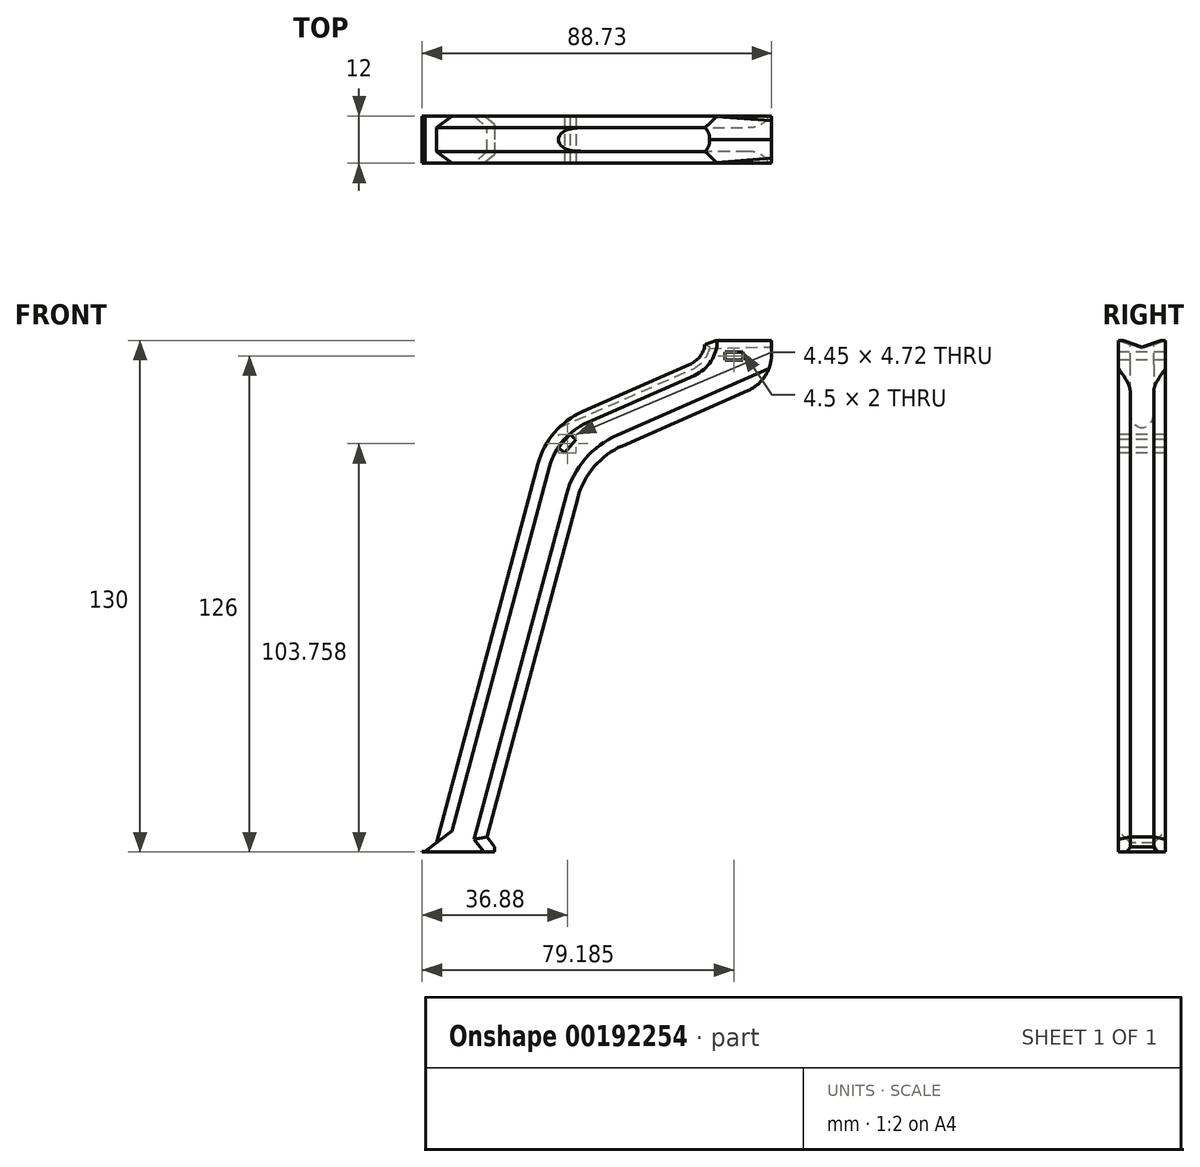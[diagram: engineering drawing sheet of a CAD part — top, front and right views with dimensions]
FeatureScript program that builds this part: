
annotation { "Feature Type Name" : "Feature", "Feature Type Description" : "" }
export const myFeature = defineFeature(function(context is Context, id is Id, definition is map)
    precondition{}
    {
        {
            var Q0;
            Q0=qCreatedBy(makeId("Front.planeOp"),FACE);
            var sketch = newSketch(context, id + "F0", { "sketchPlane" : qUnion([Q0])});
            skLineSegment(sketch, "E0", {"start": v(0, 0) * mm, "end": v(-12.42, 0) * mm});
            skLineSegment(sketch, "E1", {"start": v(-12.42, 0) * mm, "end": v(16.52, 108) * mm});
            skLineSegment(sketch, "E2", {"start": v(16.52, 108) * mm, "end": v(52.49, 123.83) * mm});
            skLineSegment(sketch, "E3", {"start": v(66.52, 130) * mm, "end": v(96.31, 130) * mm});
            skLineSegment(sketch, "E4", {"start": v(96.31, 130) * mm, "end": v(26.62, 99.33) * mm});
            skLineSegment(sketch, "E5", {"start": v(26.62, 99.33) * mm, "end": v(0, 0) * mm});
            skLineSegment(sketch, "E6", {"start": v(66.52, 130) * mm, "end": v(-16.13, 130) * mm, "construction": true});
            skCircle(sketch, "E7", {"center": v(49.77, 130) * mm, "radius": 6.74 * mm});
            skLineSegment(sketch, "E8", {"start": v(66.52, 130) * mm, "end": v(56.52, 130) * mm});
            skSolve(sketch);
        }
        {
            var Q0;
            Q0=makeQuery(id+"F0.imprint","IMPRINT",FACE,{"disambiguationData":[TD([[makeQuery(id+"F0.imprint","IMPRINT",EDGE,{"derivedFrom":sQuery(id+"F0.wireOp",EDGE,"E0")}),-1.0]])]});
            extrude(context, id + "F1", {"entities" : qUnion([Q0]), "depth" : 12 * mm});
        }
        {
            var Q0;
            Q0=makeQuery(id+"F1.opExtrude","CAP_FACE",FACE,{"disambiguationData":[OSD([sQuery(id+"F0.wireOp",EDGE,"E0"),sQuery(id+"F0.wireOp",EDGE,"E1"),sQuery(id+"F0.wireOp",EDGE,"E2"),sQuery(id+"F0.wireOp",EDGE,"E3"),sQuery(id+"F0.wireOp",EDGE,"E4"),sQuery(id+"F0.wireOp",EDGE,"E5")])],"isStart":false});
            var sketch = newSketch(context, id + "F2", { "sketchPlane" : qUnion([Q0])});
            skLineSegment(sketch, "E9.0.0", {"start": v(-12.42, 0) * mm, "end": v(0, 0) * mm});
            skLineSegment(sketch, "E9.0.1", {"start": v(0, 0) * mm, "end": v(26.62, 99.33) * mm});
            skLineSegment(sketch, "E9.0.2", {"start": v(26.62, 99.33) * mm, "end": v(96.31, 130) * mm});
            skLineSegment(sketch, "E9.0.3", {"start": v(96.31, 130) * mm, "end": v(56.52, 130) * mm});
            skLineSegment(sketch, "E9.0.4", {"start": v(66.52, 130) * mm, "end": v(16.52, 108) * mm});
            skLineSegment(sketch, "E9.0.5", {"start": v(16.52, 108) * mm, "end": v(-12.42, 0) * mm});
            skLineSegment(sketch, "E10", {"start": v(84.27, 124.7) * mm, "end": v(54.47, 124.7) * mm});
            skSolve(sketch);
        }
        {
            var Q0;
            Q0=makeQuery(id+"F1.opExtrude","CAP_FACE",FACE,{"disambiguationData":[OSD([sQuery(id+"F0.wireOp",EDGE,"E0"),sQuery(id+"F0.wireOp",EDGE,"E1"),sQuery(id+"F0.wireOp",EDGE,"E2"),sQuery(id+"F0.wireOp",EDGE,"E3"),sQuery(id+"F0.wireOp",EDGE,"E4"),sQuery(id+"F0.wireOp",EDGE,"E5")])],"isStart":false});
            var sketch = newSketch(context, id + "F3", { "sketchPlane" : qUnion([Q0])});
            skPoint(sketch, "E11.endSnap0", {"position": v(34.5, 115.91) * mm});
            skLineSegment(sketch, "E12", {"start": v(22.17, 106.12) * mm, "end": v(23.68, 104.81) * mm});
            skLineSegment(sketch, "E13", {"start": v(23.68, 104.81) * mm, "end": v(20.75, 101.4) * mm});
            skLineSegment(sketch, "E14", {"start": v(20.75, 101.4) * mm, "end": v(19.24, 102.7) * mm});
            skLineSegment(sketch, "E15", {"start": v(19.24, 102.7) * mm, "end": v(22.17, 106.12) * mm});
            skPoint(sketch, "E16", {"position": v(22.17, 106.12) * mm});
            skPoint(sketch, "E17.orphan", {"position": v(18.8, 109) * mm});
            skLineSegment(sketch, "E18", {"start": v(16.52, 108) * mm, "end": v(33.3, 93.6) * mm, "construction": true});
            skSolve(sketch);
        }
        {
            var Q0;
            Q0=makeQuery(id+"F3.imprint","IMPRINT",FACE,{"disambiguationData":[TD([[makeQuery(id+"F3.imprint","IMPRINT",EDGE,{"derivedFrom":sQuery(id+"F3.wireOp",EDGE,"E12")}),-1.0]])]});
            extrude(context, id + "F4", {"entities" : qUnion([Q0]), "operationType" : NewBodyOperationType.REMOVE, "oppositeDirection" : true, "depth" : 25 * mm});
        }
        {
            var Q0;
            Q0=makeQuery(id+"F1.opExtrude","CAP_FACE",FACE,{"disambiguationData":[OSD([sQuery(id+"F0.wireOp",EDGE,"E0"),sQuery(id+"F0.wireOp",EDGE,"E1"),sQuery(id+"F0.wireOp",EDGE,"E2"),sQuery(id+"F0.wireOp",EDGE,"E3"),sQuery(id+"F0.wireOp",EDGE,"E4"),sQuery(id+"F0.wireOp",EDGE,"E5")])],"isStart":false});
            var sketch = newSketch(context, id + "F5", { "sketchPlane" : qUnion([Q0])});
            skLineSegment(sketch, "E19.0", {"start": v(61.52, 130) * mm, "end": v(73.52, 130) * mm});
            skLineSegment(sketch, "E20.0", {"start": v(81.02, 130) * mm, "end": v(85.52, 130) * mm});
            skLineSegment(sketch, "E21.bottom", {"start": v(61.52, 127) * mm, "end": v(66.02, 127) * mm});
            skLineSegment(sketch, "E21.top", {"start": v(61.52, 125) * mm, "end": v(66.02, 125) * mm});
            skLineSegment(sketch, "E21.left", {"start": v(61.52, 127) * mm, "end": v(61.52, 125) * mm});
            skLineSegment(sketch, "E21.right", {"start": v(66.02, 127) * mm, "end": v(66.02, 125) * mm});
            skSolve(sketch);
        }
        {
            var Q0;
            Q0=makeQuery(id+"F5.imprint","IMPRINT",FACE,{"disambiguationData":[TD([[makeQuery(id+"F5.imprint","IMPRINT",EDGE,{"derivedFrom":sQuery(id+"F5.wireOp",EDGE,"E21.bottom")}),-1.0]])]});
            extrude(context, id + "F6", {"entities" : qUnion([Q0]), "operationType" : NewBodyOperationType.REMOVE, "oppositeDirection" : true, "depth" : 25 * mm});
        }
        {
            var Q0;
            Q0=makeQuery(id+"F1.opExtrude","SWEPT_FACE",FACE,{"disambiguationData":[OSD([sQuery(id+"F0.wireOp",EDGE,"E0")])]});
            var sketch = newSketch(context, id + "F7", { "sketchPlane" : qUnion([Q0])});
            skLineSegment(sketch, "E22.bottom", {"start": v(3, 0) * mm, "end": v(-15.42, 0) * mm});
            skLineSegment(sketch, "E22.top", {"start": v(3, 12) * mm, "end": v(-15.42, 12) * mm});
            skLineSegment(sketch, "E22.left", {"start": v(3, 0) * mm, "end": v(3, 12) * mm});
            skLineSegment(sketch, "E22.right", {"start": v(-15.42, 0) * mm, "end": v(-15.42, 12) * mm});
            skSolve(sketch);
        }
        {
            var Q0;
            {var subQ0=sQuery(id+"F0.wireOp",EDGE,"E0");Q0=makeQuery(id+"F7.imprint","IMPRINT",FACE,{"disambiguationData":[TD([[makeQuery(id+"F7.imprint","IMPRINT",EDGE,{"derivedFrom":makeQuery(id+"F1.opExtrude","CAP_EDGE",EDGE,{"disambiguationData":[OSD([subQ0])],"isStart":true})}),-1.0]])]});}
            var Q1;
            Q1=makeQuery(id+"F7.imprint","IMPRINT",FACE,{"disambiguationData":[TD([[makeQuery(id+"F7.imprint","IMPRINT",EDGE,{"derivedFrom":sQuery(id+"F7.wireOp",EDGE,"E22.bottom")}),-1.0]])]});
            extrude(context, id + "F8", {"entities" : qUnion([Q0, Q1]), "operationType" : NewBodyOperationType.ADD, "oppositeDirection" : true, "depth" : 0.1 * mm});
        }
        {
            var Q0;
            Q0=makeQuery(id+"F8.boolean.opBoolean","INTERSECT",EDGE,{"derivedFrom":[makeQuery(id+"F1.opExtrude","CAP_FACE",FACE,{"disambiguationData":[OSD([sQuery(id+"F0.wireOp",EDGE,"E0"),sQuery(id+"F0.wireOp",EDGE,"E1"),sQuery(id+"F0.wireOp",EDGE,"E2"),sQuery(id+"F0.wireOp",EDGE,"E3"),sQuery(id+"F0.wireOp",EDGE,"E4"),sQuery(id+"F0.wireOp",EDGE,"E5")])],"isStart":false}),makeQuery(id+"F8.opExtrude","CAP_FACE",FACE,{"disambiguationData":[OSD([sQuery(id+"F7.wireOp",EDGE,"E22.bottom"),sQuery(id+"F7.wireOp",EDGE,"E22.top"),sQuery(id+"F7.wireOp",EDGE,"E22.left"),sQuery(id+"F7.wireOp",EDGE,"E22.right")])],"isStart":false})]});
            var Q1;
            Q1=makeQuery(id+"F8.boolean.opBoolean","INTERSECT",EDGE,{"derivedFrom":[makeQuery(id+"F1.opExtrude","SWEPT_FACE",FACE,{"disambiguationData":[OSD([sQuery(id+"F0.wireOp",EDGE,"E1")])]}),makeQuery(id+"F8.opExtrude","CAP_FACE",FACE,{"disambiguationData":[OSD([sQuery(id+"F7.wireOp",EDGE,"E22.bottom"),sQuery(id+"F7.wireOp",EDGE,"E22.top"),sQuery(id+"F7.wireOp",EDGE,"E22.left"),sQuery(id+"F7.wireOp",EDGE,"E22.right")])],"isStart":false})]});
            var Q2;
            Q2=makeQuery(id+"F8.boolean.opBoolean","INTERSECT",EDGE,{"derivedFrom":[makeQuery(id+"F1.opExtrude","SWEPT_FACE",FACE,{"disambiguationData":[OSD([sQuery(id+"F0.wireOp",EDGE,"E5")])]}),makeQuery(id+"F8.opExtrude","CAP_FACE",FACE,{"disambiguationData":[OSD([sQuery(id+"F7.wireOp",EDGE,"E22.bottom"),sQuery(id+"F7.wireOp",EDGE,"E22.top"),sQuery(id+"F7.wireOp",EDGE,"E22.left"),sQuery(id+"F7.wireOp",EDGE,"E22.right")])],"isStart":false})]});
            var Q3;
            Q3=makeQuery(id+"F8.boolean.opBoolean","INTERSECT",EDGE,{"derivedFrom":[makeQuery(id+"F1.opExtrude","CAP_FACE",FACE,{"disambiguationData":[OSD([sQuery(id+"F0.wireOp",EDGE,"E0"),sQuery(id+"F0.wireOp",EDGE,"E1"),sQuery(id+"F0.wireOp",EDGE,"E2"),sQuery(id+"F0.wireOp",EDGE,"E3"),sQuery(id+"F0.wireOp",EDGE,"E4"),sQuery(id+"F0.wireOp",EDGE,"E5")])],"isStart":true}),makeQuery(id+"F8.opExtrude","CAP_FACE",FACE,{"disambiguationData":[OSD([sQuery(id+"F7.wireOp",EDGE,"E22.bottom"),sQuery(id+"F7.wireOp",EDGE,"E22.top"),sQuery(id+"F7.wireOp",EDGE,"E22.left"),sQuery(id+"F7.wireOp",EDGE,"E22.right")])],"isStart":false})]});
            chamfer(context, id + "F9", {"entities" : qUnion([Q0, Q1, Q2, Q3]), "width" : 3 * mm, "tangentPropagation" : true});
        }
        {
            var Q0;
            Q0=makeQuery(id+"F1.opExtrude","SWEPT_EDGE",EDGE,{"disambiguationData":[OSD([sQuery(id+"F0.wireOp",EDGE,"E1"),sQuery(id+"F0.wireOp",EDGE,"E2")])]});
            var Q1;
            Q1=makeQuery(id+"F1.opExtrude","SWEPT_EDGE",EDGE,{"disambiguationData":[OSD([sQuery(id+"F0.wireOp",EDGE,"E4"),sQuery(id+"F0.wireOp",EDGE,"E5")])]});
            fillet(context, id + "F10", {"entities" : qUnion([Q0, Q1]), "radius" : 20 * mm, "tangentPropagation" : true, "allowEdgeOverflow" : false});
        }
        {
            var Q0;
            Q0=makeQuery(id+"F1.opExtrude","CAP_EDGE",EDGE,{"disambiguationData":[OSD([sQuery(id+"F0.wireOp",EDGE,"E1")])],"isStart":false});
            var Q1;
            Q1=makeQuery(id+"F1.opExtrude","CAP_EDGE",EDGE,{"disambiguationData":[OSD([sQuery(id+"F0.wireOp",EDGE,"E5")])],"isStart":false});
            var Q2;
            Q2=makeQuery(id+"F1.opExtrude","CAP_EDGE",EDGE,{"disambiguationData":[OSD([sQuery(id+"F0.wireOp",EDGE,"E5")])],"isStart":true});
            var Q3;
            Q3=makeQuery(id+"F1.opExtrude","CAP_EDGE",EDGE,{"disambiguationData":[OSD([sQuery(id+"F0.wireOp",EDGE,"E1")])],"isStart":true});
            chamfer(context, id + "F11", {"entities" : qUnion([Q0, Q1, Q2, Q3]), "width" : 3 * mm, "tangentPropagation" : true});
        }
        {
            var Q0;
            {var subQ0=sQuery(id+"F7.wireOp",EDGE,"E22.bottom");var subQ1=sQuery(id+"F0.wireOp",EDGE,"E5");Q0=makeQuery(id+"F9.opChamfer","BLEND_EDGE",EDGE,{"blendedFrom":[makeQuery(id+"F8.boolean.opBoolean","INTERSECT",EDGE,{"derivedFrom":[makeQuery(id+"F1.opExtrude","SWEPT_FACE",FACE,{"disambiguationData":[OSD([subQ1])]}),makeQuery(id+"F8.opExtrude","CAP_FACE",FACE,{"disambiguationData":[OSD([subQ0,sQuery(id+"F7.wireOp",EDGE,"E22.top"),sQuery(id+"F7.wireOp",EDGE,"E22.left"),sQuery(id+"F7.wireOp",EDGE,"E22.right")])],"isStart":false})]}),makeQuery(id+"F8.boolean.opBoolean","MERGE",FACE,{"derivedFrom":[makeQuery(id+"F1.opExtrude","CAP_FACE",FACE,{"disambiguationData":[OSD([sQuery(id+"F0.wireOp",EDGE,"E0"),sQuery(id+"F0.wireOp",EDGE,"E1"),sQuery(id+"F0.wireOp",EDGE,"E2"),sQuery(id+"F0.wireOp",EDGE,"E3"),sQuery(id+"F0.wireOp",EDGE,"E4"),subQ1])],"isStart":true}),makeQuery(id+"F8.opExtrude","SWEPT_FACE",FACE,{"disambiguationData":[OSD([subQ0])]})]})],"blendedInto":[makeQuery(id+"F8.boolean.opBoolean","MERGE",FACE,{"derivedFrom":[makeQuery(id+"F1.opExtrude","CAP_FACE",FACE,{"disambiguationData":[OSD([sQuery(id+"F0.wireOp",EDGE,"E0"),sQuery(id+"F0.wireOp",EDGE,"E1"),sQuery(id+"F0.wireOp",EDGE,"E2"),sQuery(id+"F0.wireOp",EDGE,"E3"),sQuery(id+"F0.wireOp",EDGE,"E4"),subQ1])],"isStart":true}),makeQuery(id+"F8.opExtrude","SWEPT_FACE",FACE,{"disambiguationData":[OSD([subQ0])]})]})]});}
            var Q1;
            {var subQ0=sQuery(id+"F7.wireOp",EDGE,"E22.top");var subQ1=sQuery(id+"F0.wireOp",EDGE,"E5");Q1=makeQuery(id+"F9.opChamfer","BLEND_EDGE",EDGE,{"blendedFrom":[makeQuery(id+"F8.boolean.opBoolean","INTERSECT",EDGE,{"derivedFrom":[makeQuery(id+"F1.opExtrude","SWEPT_FACE",FACE,{"disambiguationData":[OSD([subQ1])]}),makeQuery(id+"F8.opExtrude","CAP_FACE",FACE,{"disambiguationData":[OSD([sQuery(id+"F7.wireOp",EDGE,"E22.bottom"),subQ0,sQuery(id+"F7.wireOp",EDGE,"E22.left"),sQuery(id+"F7.wireOp",EDGE,"E22.right")])],"isStart":false})]}),makeQuery(id+"F8.boolean.opBoolean","MERGE",FACE,{"derivedFrom":[makeQuery(id+"F1.opExtrude","CAP_FACE",FACE,{"disambiguationData":[OSD([sQuery(id+"F0.wireOp",EDGE,"E0"),sQuery(id+"F0.wireOp",EDGE,"E1"),sQuery(id+"F0.wireOp",EDGE,"E2"),sQuery(id+"F0.wireOp",EDGE,"E3"),sQuery(id+"F0.wireOp",EDGE,"E4"),subQ1])],"isStart":false}),makeQuery(id+"F8.opExtrude","SWEPT_FACE",FACE,{"disambiguationData":[OSD([subQ0])]})]})],"blendedInto":[makeQuery(id+"F8.boolean.opBoolean","MERGE",FACE,{"derivedFrom":[makeQuery(id+"F1.opExtrude","CAP_FACE",FACE,{"disambiguationData":[OSD([sQuery(id+"F0.wireOp",EDGE,"E0"),sQuery(id+"F0.wireOp",EDGE,"E1"),sQuery(id+"F0.wireOp",EDGE,"E2"),sQuery(id+"F0.wireOp",EDGE,"E3"),sQuery(id+"F0.wireOp",EDGE,"E4"),subQ1])],"isStart":false}),makeQuery(id+"F8.opExtrude","SWEPT_FACE",FACE,{"disambiguationData":[OSD([subQ0])]})]})]});}
            chamfer(context, id + "F12", {"entities" : qUnion([Q0, Q1]), "width" : 3 * mm, "tangentPropagation" : true});
        }
        {
            var Q0;
            Q0=makeQuery(id+"F1.opExtrude","SWEPT_FACE",FACE,{"disambiguationData":[OSD([sQuery(id+"F0.wireOp",EDGE,"E3"),sQuery(id+"F0.wireOp",EDGE,"E8")])]});
            var sketch = newSketch(context, id + "F13", { "sketchPlane" : qUnion([Q0])});
            skLineSegment(sketch, "E23", {"start": v(73.31, -12) * mm, "end": v(73.31, 0) * mm});
            skSolve(sketch);
        }
        {
            var Q0;
            {var subQ6=sQuery(id+"F13.wireOp",EDGE,"E23");Q0=makeQuery(id+"F13.imprint","IMPRINT",FACE,{"disambiguationData":[TD([[makeQuery(id+"F13.imprint","IMPRINT",EDGE,{"derivedFrom":subQ6}),-1.0]])]});}
            extrude(context, id + "F14", {"entities" : qUnion([Q0]), "operationType" : NewBodyOperationType.REMOVE, "oppositeDirection" : true, "depth" : 25 * mm});
        }
        {
            var Q0;
            Q0=makeQuery(id+"F14.boolean.opBoolean","INTERSECT",EDGE,{"derivedFrom":[makeQuery(id+"F1.opExtrude","SWEPT_FACE",FACE,{"disambiguationData":[OSD([sQuery(id+"F0.wireOp",EDGE,"E4")])]}),makeQuery(id+"F14.opExtrude","SWEPT_FACE",FACE,{"disambiguationData":[OSD([sQuery(id+"F13.wireOp",EDGE,"E23")])]})]});
            fillet(context, id + "F15", {"entities" : qUnion([Q0]), "radius" : 10 * mm, "tangentPropagation" : true, "allowEdgeOverflow" : false});
        }
        {
            var Q0;
            {var subQ0=sQuery(id+"F0.wireOp",EDGE,"E2");var subQ1=sQuery(id+"F0.wireOp",EDGE,"E1");Q0=makeQuery(id+"F11.opChamfer","BLEND_VERTEX",VERTEX,{"blendedFrom":[makeQuery(id+"F10.opFillet","BLEND_EDGE",EDGE,{"blendedFrom":[makeQuery(id+"F1.opExtrude","SWEPT_EDGE",EDGE,{"disambiguationData":[OSD([subQ1,subQ0])]}),makeQuery(id+"F8.boolean.opBoolean","MERGE",FACE,{"derivedFrom":[makeQuery(id+"F1.opExtrude","CAP_FACE",FACE,{"disambiguationData":[OSD([sQuery(id+"F0.wireOp",EDGE,"E0"),subQ1,subQ0,sQuery(id+"F0.wireOp",EDGE,"E3"),sQuery(id+"F0.wireOp",EDGE,"E4"),sQuery(id+"F0.wireOp",EDGE,"E5")])],"isStart":false}),makeQuery(id+"F8.opExtrude","SWEPT_FACE",FACE,{"disambiguationData":[OSD([sQuery(id+"F7.wireOp",EDGE,"E22.top")])]})]})],"blendedInto":[makeQuery(id+"F8.boolean.opBoolean","MERGE",FACE,{"derivedFrom":[makeQuery(id+"F1.opExtrude","CAP_FACE",FACE,{"disambiguationData":[OSD([sQuery(id+"F0.wireOp",EDGE,"E0"),subQ1,subQ0,sQuery(id+"F0.wireOp",EDGE,"E3"),sQuery(id+"F0.wireOp",EDGE,"E4"),sQuery(id+"F0.wireOp",EDGE,"E5")])],"isStart":false}),makeQuery(id+"F8.opExtrude","SWEPT_FACE",FACE,{"disambiguationData":[OSD([sQuery(id+"F7.wireOp",EDGE,"E22.top")])]})]})]}),makeQuery(id+"F1.opExtrude","CAP_EDGE",EDGE,{"disambiguationData":[OSD([subQ0])],"isStart":false}),makeQuery(id+"F10.opFillet","BLEND_FACE",FACE,{"disambiguationData":[OSD([subQ1,subQ0])]}),makeQuery(id+"F1.opExtrude","SWEPT_FACE",FACE,{"disambiguationData":[OSD([subQ0])]})],"blendedInto":[makeQuery(id+"F10.opFillet","BLEND_FACE",FACE,{"disambiguationData":[OSD([subQ1,subQ0])]}),makeQuery(id+"F1.opExtrude","SWEPT_FACE",FACE,{"disambiguationData":[OSD([subQ0])]})]});}
            var Q1;
            {var subQ0=sQuery(id+"F0.wireOp",EDGE,"E2");var subQ1=sQuery(id+"F0.wireOp",EDGE,"E1");Q1=makeQuery(id+"F11.opChamfer","BLEND_VERTEX",VERTEX,{"blendedFrom":[makeQuery(id+"F10.opFillet","BLEND_EDGE",EDGE,{"blendedFrom":[makeQuery(id+"F1.opExtrude","SWEPT_EDGE",EDGE,{"disambiguationData":[OSD([subQ1,subQ0])]}),makeQuery(id+"F8.boolean.opBoolean","MERGE",FACE,{"derivedFrom":[makeQuery(id+"F1.opExtrude","CAP_FACE",FACE,{"disambiguationData":[OSD([sQuery(id+"F0.wireOp",EDGE,"E0"),subQ1,subQ0,sQuery(id+"F0.wireOp",EDGE,"E3"),sQuery(id+"F0.wireOp",EDGE,"E4"),sQuery(id+"F0.wireOp",EDGE,"E5")])],"isStart":true}),makeQuery(id+"F8.opExtrude","SWEPT_FACE",FACE,{"disambiguationData":[OSD([sQuery(id+"F7.wireOp",EDGE,"E22.bottom")])]})]})],"blendedInto":[makeQuery(id+"F8.boolean.opBoolean","MERGE",FACE,{"derivedFrom":[makeQuery(id+"F1.opExtrude","CAP_FACE",FACE,{"disambiguationData":[OSD([sQuery(id+"F0.wireOp",EDGE,"E0"),subQ1,subQ0,sQuery(id+"F0.wireOp",EDGE,"E3"),sQuery(id+"F0.wireOp",EDGE,"E4"),sQuery(id+"F0.wireOp",EDGE,"E5")])],"isStart":true}),makeQuery(id+"F8.opExtrude","SWEPT_FACE",FACE,{"disambiguationData":[OSD([sQuery(id+"F7.wireOp",EDGE,"E22.bottom")])]})]})]}),makeQuery(id+"F1.opExtrude","CAP_EDGE",EDGE,{"disambiguationData":[OSD([subQ0])],"isStart":true}),makeQuery(id+"F10.opFillet","BLEND_FACE",FACE,{"disambiguationData":[OSD([subQ1,subQ0])]}),makeQuery(id+"F1.opExtrude","SWEPT_FACE",FACE,{"disambiguationData":[OSD([subQ0])]})],"blendedInto":[makeQuery(id+"F10.opFillet","BLEND_FACE",FACE,{"disambiguationData":[OSD([subQ1,subQ0])]}),makeQuery(id+"F1.opExtrude","SWEPT_FACE",FACE,{"disambiguationData":[OSD([subQ0])]})]});}
            var Q2;
            {var subQ0=sQuery(id+"F0.wireOp",EDGE,"E2");var subQ1=sQuery(id+"F0.wireOp",EDGE,"E1");var subQ2=makeQuery(id+"F8.boolean.opBoolean","MERGE",FACE,{"derivedFrom":[makeQuery(id+"F1.opExtrude","CAP_FACE",FACE,{"disambiguationData":[OSD([sQuery(id+"F0.wireOp",EDGE,"E0"),subQ1,subQ0,sQuery(id+"F0.wireOp",EDGE,"E3"),sQuery(id+"F0.wireOp",EDGE,"E4"),sQuery(id+"F0.wireOp",EDGE,"E5")])],"isStart":false}),makeQuery(id+"F8.opExtrude","SWEPT_FACE",FACE,{"disambiguationData":[OSD([sQuery(id+"F7.wireOp",EDGE,"E22.top")])]})]});Q2=makeQuery(id+"F11.opChamfer","BLEND_VERTEX",VERTEX,{"blendedFrom":[makeQuery(id+"F10.opFillet","BLEND_EDGE",EDGE,{"blendedFrom":[makeQuery(id+"F1.opExtrude","SWEPT_EDGE",EDGE,{"disambiguationData":[OSD([subQ1,subQ0])]}),subQ2],"blendedInto":[subQ2]}),makeQuery(id+"F1.opExtrude","CAP_EDGE",EDGE,{"disambiguationData":[OSD([subQ0])],"isStart":false}),subQ2],"blendedInto":[subQ2]});}
            cPlane(context, id + "F16", {"entities" : qUnion([Q0, Q1, Q2]), "cplaneType" : CPlaneType.THREE_POINT, "offset" : 25 * mm, "width" : 150 * mm, "height" : 150 * mm});
        }
        {
            var Q0;
            Q0=qCreatedBy(id+"F16.planeOp",FACE);
            var sketch = newSketch(context, id + "F17", { "sketchPlane" : qUnion([Q0])});
            skLineSegment(sketch, "E24.0", {"start": v(-3, 92.2) * mm, "end": v(-9, 92.2) * mm});
            skArc(sketch, "E25", {"start": v(-9, 92.2) * mm, "mid": v(-6, 90.85) * mm, "end": v(-3, 92.2) * mm});
            skSolve(sketch);
        }
        {
            var Q0;
            Q0=makeQuery(id+"F17.imprint","IMPRINT",FACE,{"disambiguationData":[TD([[makeQuery(id+"F17.imprint","IMPRINT",EDGE,{"derivedFrom":sQuery(id+"F17.wireOp",EDGE,"E24.0")}),1.0]])]});
            var Q1;
            {var subQ0=sQuery(id+"F0.wireOp",EDGE,"E2");Q1=makeQuery(id+"F11.opChamfer","BLEND_EDGE",EDGE,{"blendedFrom":[makeQuery(id+"F1.opExtrude","CAP_EDGE",EDGE,{"disambiguationData":[OSD([subQ0])],"isStart":false}),makeQuery(id+"F1.opExtrude","SWEPT_FACE",FACE,{"disambiguationData":[OSD([subQ0])]})],"blendedInto":[makeQuery(id+"F1.opExtrude","SWEPT_FACE",FACE,{"disambiguationData":[OSD([subQ0])]})]});}
            var Q2;
            {var subQ0=sQuery(id+"F0.wireOp",EDGE,"E7");Q2=makeQuery(id+"F11.opChamfer","BLEND_EDGE",EDGE,{"blendedFrom":[makeQuery(id+"F1.opExtrude","CAP_EDGE",EDGE,{"disambiguationData":[OSD([subQ0])],"isStart":false}),makeQuery(id+"F1.opExtrude","SWEPT_FACE",FACE,{"disambiguationData":[OSD([subQ0])]})],"blendedInto":[makeQuery(id+"F1.opExtrude","SWEPT_FACE",FACE,{"disambiguationData":[OSD([subQ0])]})]});}
            sweep(context, id + "F18", {"operationType" : NewBodyOperationType.REMOVE, "profiles" : qUnion([Q0]), "path" : qUnion([Q1, Q2])});
        }
        {
            var Q0;
            Q0=makeQuery(id+"F18.boolean.opBoolean","COPY",FACE,{"derivedFrom":makeQuery(id+"F18.opSweep","CAP_FACE",FACE,{"disambiguationData":[OSD([sQuery(id+"F0.wireOp",EDGE,"E0"),sQuery(id+"F0.wireOp",EDGE,"E1"),sQuery(id+"F0.wireOp",EDGE,"E2"),sQuery(id+"F0.wireOp",EDGE,"E3"),sQuery(id+"F0.wireOp",EDGE,"E4"),sQuery(id+"F0.wireOp",EDGE,"E5"),sQuery(id+"F0.wireOp",EDGE,"E7"),sQuery(id+"F0.wireOp",EDGE,"E8"),sQuery(id+"F7.wireOp",EDGE,"E22.top"),sQuery(id+"F17.wireOp",EDGE,"E24.0"),sQuery(id+"F17.wireOp",EDGE,"E25")])],"isStart":true})});
            extrude(context, id + "F19", {"entities" : qUnion([Q0]), "operationType" : NewBodyOperationType.REMOVE, "oppositeDirection" : true, "depth" : 25 * mm});
        }
        {
            var Q0;
            Q0=makeQuery(id+"F14.boolean.opBoolean","COPY",FACE,{"derivedFrom":makeQuery(id+"F14.opExtrude","SWEPT_FACE",FACE,{"disambiguationData":[OSD([sQuery(id+"F13.wireOp",EDGE,"E23")])]})});
            var sketch = newSketch(context, id + "F20", { "sketchPlane" : qUnion([Q0])});
            skLineSegment(sketch, "E26", {"start": v(-6, 128.34) * mm, "end": v(-14.5, 131.3) * mm});
            skLineSegment(sketch, "E27", {"start": v(-14.5, 131.3) * mm, "end": v(2.5, 131.3) * mm});
            skLineSegment(sketch, "E28", {"start": v(2.5, 131.3) * mm, "end": v(-6, 128.34) * mm});
            skLineSegment(sketch, "E29", {"start": v(-6, 130) * mm, "end": v(-6, 141.69) * mm});
            skSolve(sketch);
        }
        {
            var Q0;
            {var subQ0=sQuery(id+"F20.wireOp",EDGE,"E28");var subQ1=sQuery(id+"F20.wireOp",EDGE,"E26");var subQ2=makeQuery(id+"F20.imprint","INTERSECT",VERTEX,{"derivedFrom":[subQ1,subQ0]});Q0=makeQuery(id+"F20.imprint","IMPRINT",FACE,{"disambiguationData":[TD([[makeQuery(id+"F20.imprint","IMPRINT",EDGE,{"disambiguationData":[TD([[subQ2,-1.0]])],"derivedFrom":subQ1}),-1.0]])]});}
            extrude(context, id + "F21", {"entities" : qUnion([Q0]), "operationType" : NewBodyOperationType.REMOVE, "oppositeDirection" : true, "depth" : 25 * mm, "hasDraft" : true, "draftAngle" : 1.5 * degree});
        }
    });
